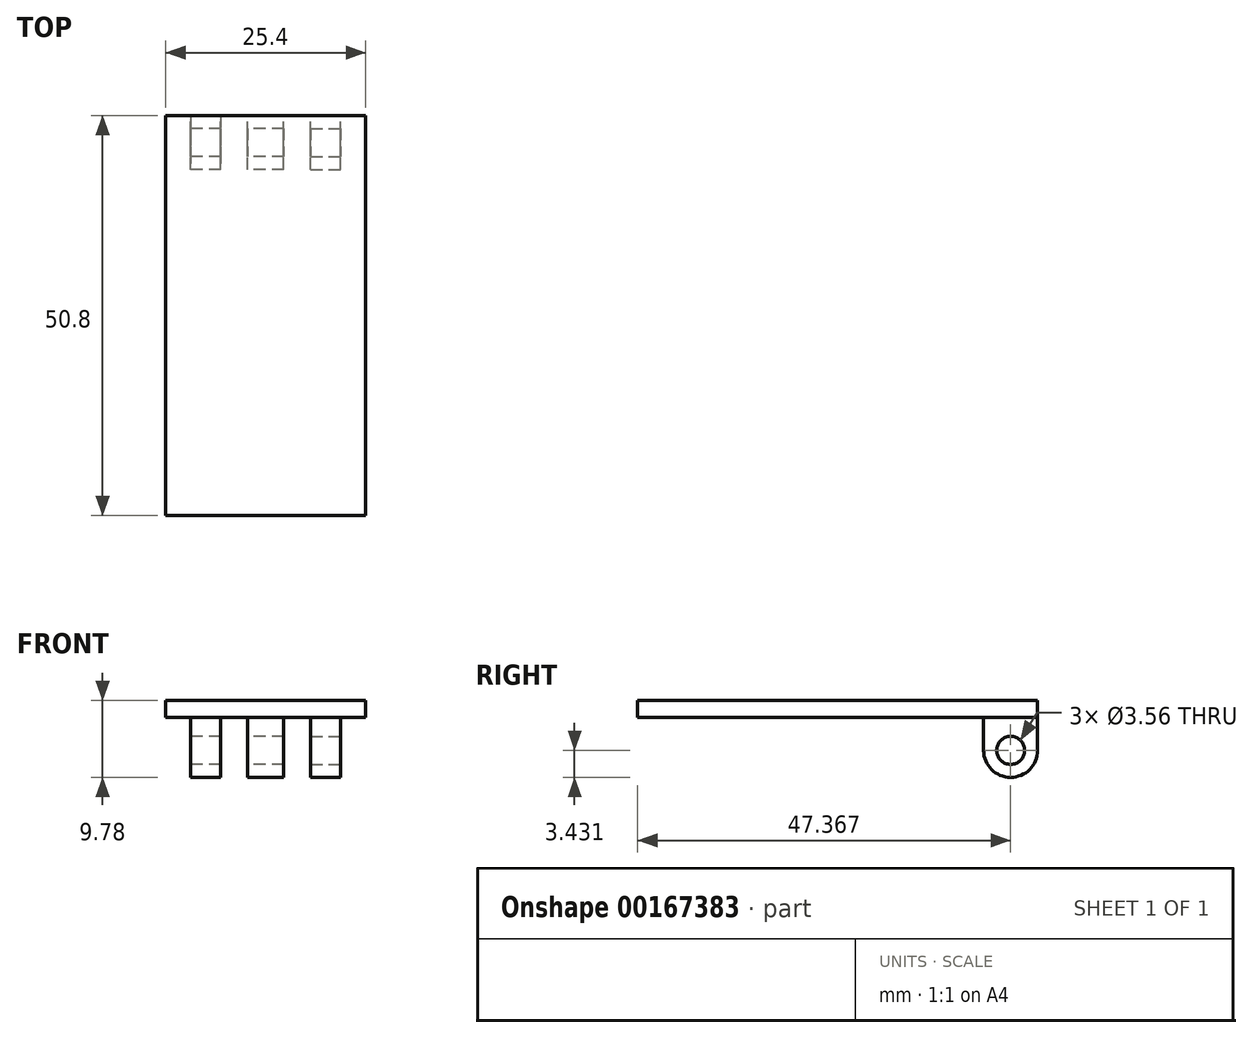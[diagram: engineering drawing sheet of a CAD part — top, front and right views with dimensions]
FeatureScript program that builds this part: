
annotation { "Feature Type Name" : "Feature", "Feature Type Description" : "" }
export const myFeature = defineFeature(function(context is Context, id is Id, definition is map)
    precondition{}
    {
        {
            var Q0;
            Q0=qCreatedBy(makeId("Right.planeOp"),FACE);
            var sketch = newSketch(context, id + "F0", { "sketchPlane" : qUnion([Q0])});
            skLineSegment(sketch, "E0.bottom", {"start": v(-30.53, 17.97) * mm, "end": v(20.27, 17.97) * mm});
            skLineSegment(sketch, "E0.top", {"start": v(-30.53, 15.81) * mm, "end": v(20.27, 15.81) * mm});
            skLineSegment(sketch, "E0.left", {"start": v(-30.53, 17.97) * mm, "end": v(-30.53, 15.81) * mm});
            skLineSegment(sketch, "E0.right", {"start": v(20.27, 17.97) * mm, "end": v(20.27, 15.81) * mm});
            skCircle(sketch, "E1", {"center": v(16.84, 11.62) * mm, "radius": 1.78 * mm});
            skCircle(sketch, "E2", {"center": v(16.84, 11.62) * mm, "radius": 3.43 * mm});
            skLineSegment(sketch, "E3", {"start": v(20.27, 11.62) * mm, "end": v(20.27, 15.81) * mm});
            skLineSegment(sketch, "E4", {"start": v(13.4, 11.62) * mm, "end": v(13.4, 15.81) * mm});
            skSolve(sketch);
        }
        {
            var Q0;
            Q0=makeQuery(id+"F0.imprint","IMPRINT",FACE,{"disambiguationData":[TD([[makeQuery(id+"F0.imprint","IMPRINT",EDGE,{"derivedFrom":sQuery(id+"F0.wireOp",EDGE,"E0.bottom")}),-1.0]])]});
            extrude(context, id + "F1", {"entities" : qUnion([Q0]), "depth" : 12.7 * mm, "hasSecondDirection" : true, "secondDirectionOppositeDirection" : true, "secondDirectionDepth" : 12.7 * mm});
        }
        {
            var Q0;
            {var subQ0=sQuery(id+"F0.wireOp",EDGE,"E3");Q0=makeQuery(id+"F0.imprint","IMPRINT",FACE,{"disambiguationData":[TD([[makeQuery(id+"F0.imprint","IMPRINT",EDGE,{"derivedFrom":subQ0}),1.0]])]});}
            var Q1;
            Q1=makeQuery(id+"F0.imprint","IMPRINT",FACE,{"disambiguationData":[TD([[makeQuery(id+"F0.imprint","IMPRINT",EDGE,{"derivedFrom":sQuery(id+"F0.wireOp",EDGE,"E1")}),-1.0]])]});
            extrude(context, id + "F2", {"entities" : qUnion([Q0, Q1]), "operationType" : NewBodyOperationType.ADD, "depth" : 2.3 * mm, "hasSecondDirection" : true, "secondDirectionOppositeDirection" : true, "secondDirectionDepth" : 2.3 * mm});
        }
        {
            var Q0;
            Q0=makeQuery(id+"F1.opExtrude","CAP_FACE",FACE,{"disambiguationData":[OSD([sQuery(id+"F0.wireOp",EDGE,"E0.bottom"),sQuery(id+"F0.wireOp",EDGE,"E0.top"),sQuery(id+"F0.wireOp",EDGE,"E0.left"),sQuery(id+"F0.wireOp",EDGE,"E0.right")])],"isStart":false});
            cPlane(context, id + "F3", {"entities" : qUnion([Q0]), "cplaneType" : CPlaneType.OFFSET, "offset" : 3.17 * mm, "oppositeDirection" : true, "width" : 152.4 * mm, "height" : 152.4 * mm});
        }
        {
            var Q0;
            Q0=qCreatedBy(id+"F3.planeOp",FACE);
            var sketch = newSketch(context, id + "F4", { "sketchPlane" : qUnion([Q0])});
            skLineSegment(sketch, "E5.0", {"start": v(13.4, 15.81) * mm, "end": v(20.27, 15.81) * mm});
            skArc(sketch, "E6.0", {"start": v(13.4, 11.62) * mm, "mid": v(16.84, 8.2) * mm, "end": v(20.27, 11.62) * mm});
            skCircle(sketch, "E6.1", {"center": v(16.84, 11.62) * mm, "radius": 1.78 * mm});
            skLineSegment(sketch, "E6.2", {"start": v(20.27, 11.62) * mm, "end": v(20.27, 15.81) * mm});
            skLineSegment(sketch, "E6.3", {"start": v(13.4, 11.62) * mm, "end": v(13.4, 15.81) * mm});
            skSolve(sketch);
        }
        {
            var Q0;
            Q0 = qSketchRegion(id + "F4", true);
            extrude(context, id + "F5", {"entities" : qUnion([Q0]), "operationType" : NewBodyOperationType.ADD, "oppositeDirection" : true, "depth" : 3.8 * mm});
        }
        {
            var Q0;
            Q0=makeQuery(id+"F1.opExtrude","CAP_FACE",FACE,{"disambiguationData":[OSD([sQuery(id+"F0.wireOp",EDGE,"E0.bottom"),sQuery(id+"F0.wireOp",EDGE,"E0.top"),sQuery(id+"F0.wireOp",EDGE,"E0.left"),sQuery(id+"F0.wireOp",EDGE,"E0.right")])],"isStart":true});
            cPlane(context, id + "F6", {"entities" : qUnion([Q0]), "cplaneType" : CPlaneType.OFFSET, "offset" : 3.17 * mm, "oppositeDirection" : true, "width" : 152.4 * mm, "height" : 152.4 * mm});
        }
        {
            var Q0;
            Q0=qCreatedBy(id+"F6.planeOp",FACE);
            var sketch = newSketch(context, id + "F7", { "sketchPlane" : qUnion([Q0])});
            skLineSegment(sketch, "E7.0", {"start": v(-13.4, 15.81) * mm, "end": v(-20.27, 15.81) * mm});
            skArc(sketch, "E7.1", {"start": v(-13.4, 11.62) * mm, "mid": v(-16.84, 8.2) * mm, "end": v(-20.27, 11.62) * mm});
            skCircle(sketch, "E7.2", {"center": v(-16.84, 11.62) * mm, "radius": 1.78 * mm});
            skLineSegment(sketch, "E7.3", {"start": v(-13.4, 11.62) * mm, "end": v(-13.4, 15.81) * mm});
            skLineSegment(sketch, "E7.4", {"start": v(-20.27, 11.62) * mm, "end": v(-20.27, 15.81) * mm});
            skSolve(sketch);
        }
        {
            var Q0;
            Q0 = qSketchRegion(id + "F7", true);
            extrude(context, id + "F8", {"entities" : qUnion([Q0]), "operationType" : NewBodyOperationType.ADD, "oppositeDirection" : true, "depth" : 3.8 * mm});
        }
    });
